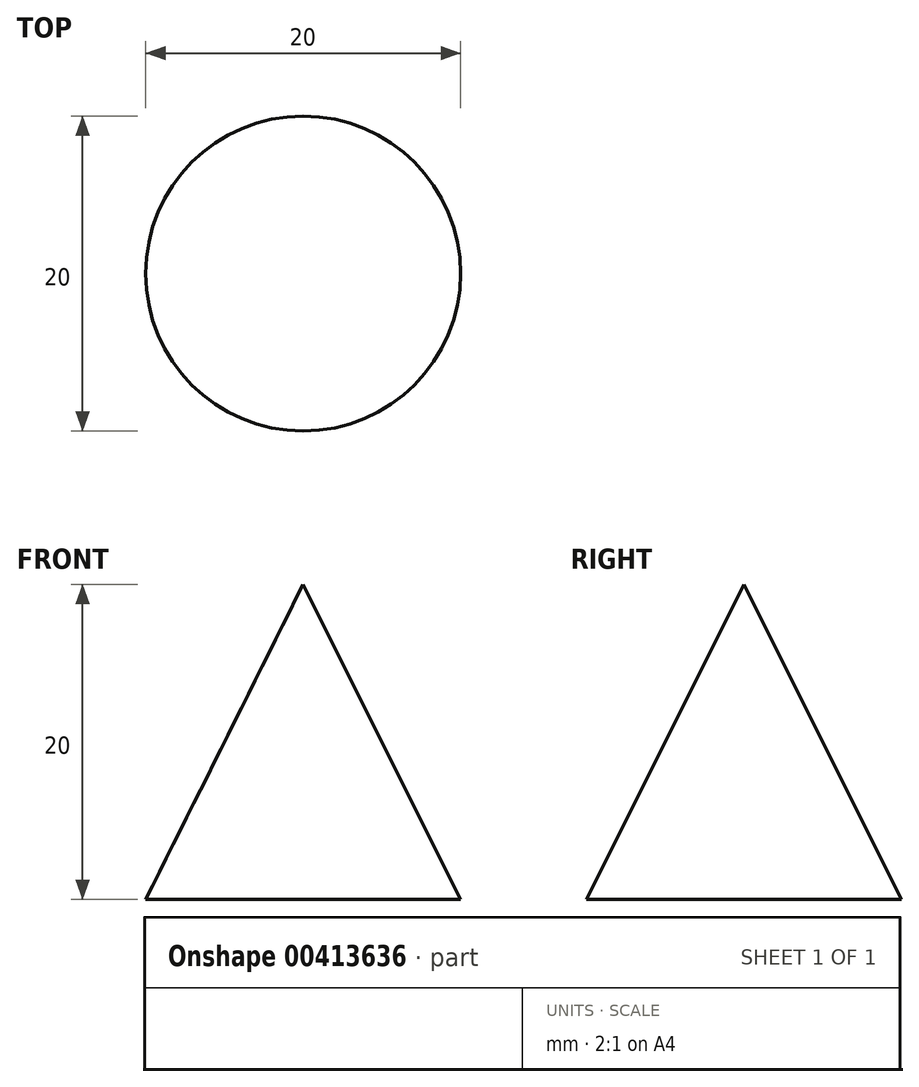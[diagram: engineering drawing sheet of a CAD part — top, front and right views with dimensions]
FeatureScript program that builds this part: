
annotation { "Feature Type Name" : "Feature", "Feature Type Description" : "" }
export const myFeature = defineFeature(function(context is Context, id is Id, definition is map)
    precondition{}
    {
        {
            var Q0;
            Q0=qCreatedBy(makeId("Front.planeOp"),FACE);
            var sketch = newSketch(context, id + "F0", { "sketchPlane" : qUnion([Q0])});
            skLineSegment(sketch, "E0", {"start": v(0, 0) * mm, "end": v(0, 20) * mm});
            skLineSegment(sketch, "E1", {"start": v(0, 0) * mm, "end": v(10, 0) * mm});
            skLineSegment(sketch, "E2", {"start": v(0, 20) * mm, "end": v(10, 0) * mm});
            skSolve(sketch);
        }
        {
            var Q0;
            Q0 = qSketchRegion(id + "F0", true);
            var Q1;
            Q1=sQuery(id+"F0.wireOp",EDGE,"E0");
            revolve(context, id + "F1", {"entities" : qUnion([Q0]), "axis" : qUnion([Q1]), "revolveType" : RevolveType.FULL});
        }
    });
